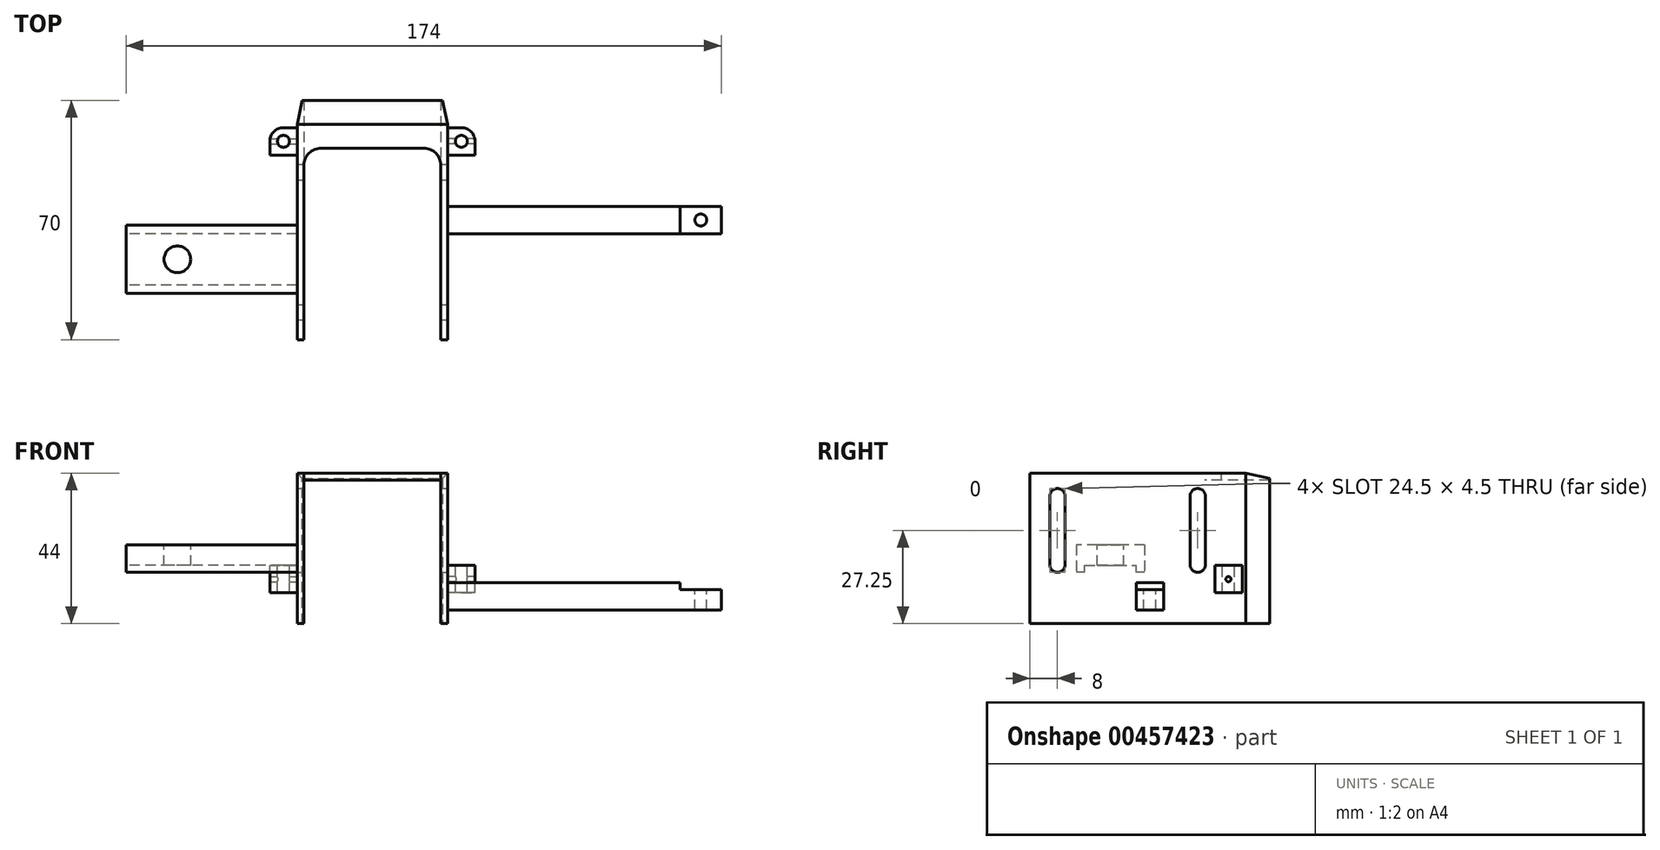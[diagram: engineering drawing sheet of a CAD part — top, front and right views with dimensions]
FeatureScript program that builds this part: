
annotation { "Feature Type Name" : "Feature", "Feature Type Description" : "" }
export const myFeature = defineFeature(function(context is Context, id is Id, definition is map)
    precondition{}
    {
        {
            var Q0;
            Q0=qCreatedBy(makeId("Front.planeOp"),FACE);
            var sketch = newSketch(context, id + "F0", { "sketchPlane" : qUnion([Q0])});
            skLineSegment(sketch, "E0.bottom", {"start": v(0, 0) * mm, "end": v(44, 0) * mm});
            skLineSegment(sketch, "E0.top", {"start": v(0, 44) * mm, "end": v(44, 44) * mm});
            skLineSegment(sketch, "E0.left", {"start": v(0, 0) * mm, "end": v(0, 44) * mm});
            skLineSegment(sketch, "E0.right", {"start": v(44, 0) * mm, "end": v(44, 44) * mm});
            skSolve(sketch);
        }
        {
            var Q0;
            Q0 = qSketchRegion(id + "F0", true);
            extrude(context, id + "F1", {"entities" : qUnion([Q0]), "oppositeDirection" : true, "depth" : 70 * mm});
        }
        {
            var Q0;
            Q0=makeQuery(id+"F1.opExtrude","CAP_FACE",FACE,{"disambiguationData":[OSD([sQuery(id+"F0.wireOp",EDGE,"E0.bottom"),sQuery(id+"F0.wireOp",EDGE,"E0.top"),sQuery(id+"F0.wireOp",EDGE,"E0.left"),sQuery(id+"F0.wireOp",EDGE,"E0.right")])],"isStart":true});
            var sketch = newSketch(context, id + "F2", { "sketchPlane" : qUnion([Q0])});
            skLineSegment(sketch, "E1.bottom", {"start": v(2, 0) * mm, "end": v(42, 0) * mm});
            skLineSegment(sketch, "E1.top", {"start": v(2, 42) * mm, "end": v(42, 42) * mm});
            skLineSegment(sketch, "E1.left", {"start": v(2, 0) * mm, "end": v(2, 42) * mm});
            skLineSegment(sketch, "E1.right", {"start": v(42, 0) * mm, "end": v(42, 42) * mm});
            skSolve(sketch);
        }
        {
            var Q0;
            Q0 = qSketchRegion(id + "F2", true);
            extrude(context, id + "F3", {"entities" : qUnion([Q0]), "operationType" : NewBodyOperationType.REMOVE, "endBound" : BoundingType.UP_TO_NEXT, "oppositeDirection" : true, "depth" : 25 * mm});
        }
        {
            var Q0;
            Q0=makeQuery(id+"F1.opExtrude","SWEPT_FACE",FACE,{"disambiguationData":[OSD([sQuery(id+"F0.wireOp",EDGE,"E0.right")])]});
            var sketch = newSketch(context, id + "F4", { "sketchPlane" : qUnion([Q0])});
            skLineSegment(sketch, "E2", {"start": v(46.75, 37.25) * mm, "end": v(46.75, 17.25) * mm});
            skLineSegment(sketch, "E3", {"start": v(51.25, 37.25) * mm, "end": v(51.25, 17.25) * mm});
            skArc(sketch, "E4", {"start": v(51.25, 37.25) * mm, "mid": v(49, 39.5) * mm, "end": v(46.75, 37.25) * mm});
            skArc(sketch, "E5", {"start": v(46.75, 17.25) * mm, "mid": v(49, 15) * mm, "end": v(51.25, 17.25) * mm});
            skSolve(sketch);
        }
        {
            var Q0;
            Q0 = qSketchRegion(id + "F4", true);
            extrude(context, id + "F5", {"entities" : qUnion([Q0]), "operationType" : NewBodyOperationType.REMOVE, "oppositeDirection" : true, "depth" : 44 * mm});
        }
        {
            var Q0;
            Q0=makeQuery(id+"F1.opExtrude","SWEPT_FACE",FACE,{"disambiguationData":[OSD([sQuery(id+"F0.wireOp",EDGE,"E0.top")])]});
            var sketch = newSketch(context, id + "F6", { "sketchPlane" : qUnion([Q0])});
            skLineSegment(sketch, "E6.bottom", {"start": v(2, 0) * mm, "end": v(42, 0) * mm});
            skLineSegment(sketch, "E6.top", {"start": v(7, 56) * mm, "end": v(37, 56) * mm});
            skLineSegment(sketch, "E6.left", {"start": v(2, 0) * mm, "end": v(2, 51) * mm});
            skLineSegment(sketch, "E6.right", {"start": v(42, 0) * mm, "end": v(42, 51) * mm});
            skPoint(sketch, "E7.visualSharp", {"position": v(2, 56) * mm});
            skArc(sketch, "E7.filletArc", {"start": v(7, 56) * mm, "mid": v(3.46, 54.54) * mm, "end": v(2, 51) * mm});
            skPoint(sketch, "E8.visualSharp", {"position": v(42, 56) * mm});
            skArc(sketch, "E8.filletArc", {"start": v(42, 51) * mm, "mid": v(40.54, 54.54) * mm, "end": v(37, 56) * mm});
            skSolve(sketch);
        }
        {
            var Q0;
            Q0=makeQuery(id+"F6.imprint","IMPRINT",FACE,{"disambiguationData":[TD([[makeQuery(id+"F6.imprint","IMPRINT",EDGE,{"derivedFrom":sQuery(id+"F6.wireOp",EDGE,"E6.bottom")}),1.0]])]});
            var Q1;
            Q1=sQuery(id+"F6.wireOp",EDGE,"E6.bottom");
            var Q2;
            Q2=sQuery(id+"F6.wireOp",EDGE,"E6.right");
            var Q3;
            Q3=sQuery(id+"F6.wireOp",EDGE,"E6.top");
            var Q4;
            Q4=sQuery(id+"F6.wireOp",EDGE,"E6.left");
            var Q5;
            Q5=sQuery(id+"F6.wireOp",EDGE,"E7.filletArc");
            var Q6;
            Q6=sQuery(id+"F6.wireOp",EDGE,"E8.filletArc");
            extrude(context, id + "F7", {"entities" : qUnion([Q0]), "operationType" : NewBodyOperationType.REMOVE, "surfaceEntities" : qUnion([Q1, Q2, Q3, Q4, Q5, Q6]), "endBound" : BoundingType.UP_TO_NEXT, "oppositeDirection" : true, "depth" : 25 * mm});
        }
        {
            var Q0;
            Q0=makeQuery(id+"F1.opExtrude","SWEPT_FACE",FACE,{"disambiguationData":[OSD([sQuery(id+"F0.wireOp",EDGE,"E0.right")])]});
            var sketch = newSketch(context, id + "F8", { "sketchPlane" : qUnion([Q0])});
            skLineSegment(sketch, "E9", {"start": v(5.75, 37.25) * mm, "end": v(5.75, 17.25) * mm});
            skLineSegment(sketch, "E10", {"start": v(10.25, 37.25) * mm, "end": v(10.25, 17.25) * mm});
            skArc(sketch, "E11", {"start": v(10.25, 37.25) * mm, "mid": v(8, 39.5) * mm, "end": v(5.75, 37.25) * mm});
            skArc(sketch, "E12", {"start": v(5.75, 17.25) * mm, "mid": v(8, 15) * mm, "end": v(10.25, 17.25) * mm});
            skSolve(sketch);
        }
        {
            var Q0;
            Q0=makeQuery(id+"F1.opExtrude","SWEPT_FACE",FACE,{"disambiguationData":[OSD([sQuery(id+"F0.wireOp",EDGE,"E0.right")])]});
            var sketch = newSketch(context, id + "F9", { "sketchPlane" : qUnion([Q0])});
            skLineSegment(sketch, "E13.bottom", {"start": v(39, 4) * mm, "end": v(31, 4) * mm});
            skLineSegment(sketch, "E13.top", {"start": v(39, 12) * mm, "end": v(31, 12) * mm});
            skLineSegment(sketch, "E13.left", {"start": v(39, 4) * mm, "end": v(39, 12) * mm});
            skLineSegment(sketch, "E13.right", {"start": v(31, 4) * mm, "end": v(31, 12) * mm});
            skPoint(sketch, "E13.middle", {"position": v(35, 8) * mm});
            skSolve(sketch);
        }
        {
            var Q0;
            Q0 = qSketchRegion(id + "F9", true);
            extrude(context, id + "F10", {"entities" : qUnion([Q0]), "operationType" : NewBodyOperationType.ADD, "depth" : 80 * mm});
        }
        {
            var Q0;
            Q0=makeQuery(id+"F10.opExtrude","CAP_FACE",FACE,{"disambiguationData":[OSD([sQuery(id+"F9.wireOp",EDGE,"E13.bottom"),sQuery(id+"F9.wireOp",EDGE,"E13.top"),sQuery(id+"F9.wireOp",EDGE,"E13.left"),sQuery(id+"F9.wireOp",EDGE,"E13.right")])],"isStart":false});
            var sketch = newSketch(context, id + "F11", { "sketchPlane" : qUnion([Q0])});
            skLineSegment(sketch, "E14.bottom", {"start": v(39, 12) * mm, "end": v(31, 12) * mm});
            skLineSegment(sketch, "E14.top", {"start": v(39, 10) * mm, "end": v(31, 10) * mm});
            skLineSegment(sketch, "E14.left", {"start": v(39, 12) * mm, "end": v(39, 10) * mm});
            skLineSegment(sketch, "E14.right", {"start": v(31, 12) * mm, "end": v(31, 10) * mm});
            skSolve(sketch);
        }
        {
            var Q0;
            Q0 = qSketchRegion(id + "F11", true);
            extrude(context, id + "F12", {"entities" : qUnion([Q0]), "operationType" : NewBodyOperationType.REMOVE, "oppositeDirection" : true, "depth" : 12 * mm});
        }
        {
            var Q0;
            Q0=makeQuery(id+"F1.opExtrude","SWEPT_FACE",FACE,{"disambiguationData":[OSD([sQuery(id+"F0.wireOp",EDGE,"E0.left")])]});
            var sketch = newSketch(context, id + "F13", { "sketchPlane" : qUnion([Q0])});
            skLineSegment(sketch, "E15.bottom", {"start": v(-33.5, 23) * mm, "end": v(-13.5, 23) * mm});
            skLineSegment(sketch, "E15.top", {"start": v(-33.5, 15) * mm, "end": v(-13.5, 15) * mm});
            skLineSegment(sketch, "E15.left", {"start": v(-33.5, 23) * mm, "end": v(-33.5, 15) * mm});
            skLineSegment(sketch, "E15.right", {"start": v(-13.5, 23) * mm, "end": v(-13.5, 15) * mm});
            skSolve(sketch);
        }
        {
            var Q0;
            Q0 = qSketchRegion(id + "F13", true);
            extrude(context, id + "F14", {"entities" : qUnion([Q0]), "operationType" : NewBodyOperationType.ADD, "depth" : 50 * mm});
        }
        {
            var Q0;
            Q0=makeQuery(id+"F14.opExtrude","CAP_FACE",FACE,{"disambiguationData":[OSD([sQuery(id+"F13.wireOp",EDGE,"E15.bottom"),sQuery(id+"F13.wireOp",EDGE,"E15.top"),sQuery(id+"F13.wireOp",EDGE,"E15.left"),sQuery(id+"F13.wireOp",EDGE,"E15.right")])],"isStart":false});
            var sketch = newSketch(context, id + "F15", { "sketchPlane" : qUnion([Q0])});
            skLineSegment(sketch, "E16.bottom", {"start": v(-16, 15) * mm, "end": v(-31, 15) * mm});
            skLineSegment(sketch, "E16.top", {"start": v(-16, 17) * mm, "end": v(-31, 17) * mm});
            skLineSegment(sketch, "E16.left", {"start": v(-16, 15) * mm, "end": v(-16, 17) * mm});
            skLineSegment(sketch, "E16.right", {"start": v(-31, 15) * mm, "end": v(-31, 17) * mm});
            skSolve(sketch);
        }
        {
            var Q0;
            Q0 = qSketchRegion(id + "F15", true);
            var Q1;
            Q1=makeQuery(id+"F1.opExtrude","SWEPT_FACE",FACE,{"disambiguationData":[OSD([sQuery(id+"F0.wireOp",EDGE,"E0.left")])]});
            extrude(context, id + "F16", {"entities" : qUnion([Q0]), "operationType" : NewBodyOperationType.REMOVE, "endBound" : BoundingType.UP_TO_SURFACE, "oppositeDirection" : true, "endBoundEntityFace" : qUnion([Q1]), "depth" : 46 * mm});
        }
        {
            var Q0;
            Q0=makeQuery(id+"F14.opExtrude","SWEPT_FACE",FACE,{"disambiguationData":[OSD([sQuery(id+"F13.wireOp",EDGE,"E15.bottom")])]});
            var sketch = newSketch(context, id + "F17", { "sketchPlane" : qUnion([Q0])});
            skCircle(sketch, "E17", {"center": v(-35, 23.5) * mm, "radius": 3.9 * mm});
            skPoint(sketch, "E17.centerSnap0", {"position": v(-50, 23.5) * mm});
            skSolve(sketch);
        }
        {
            var Q0;
            Q0 = qSketchRegion(id + "F17", true);
            extrude(context, id + "F18", {"entities" : qUnion([Q0]), "operationType" : NewBodyOperationType.REMOVE, "oppositeDirection" : true, "depth" : 20 * mm});
        }
        {
            var Q0;
            Q0=makeQuery(id+"F1.opExtrude","CAP_EDGE",EDGE,{"disambiguationData":[OSD([sQuery(id+"F0.wireOp",EDGE,"E0.right")])],"isStart":false});
            chamfer(context, id + "F19", {"entities" : qUnion([Q0]), "chamferType" : ChamferType.TWO_OFFSETS, "width1" : 7 * mm, "oppositeDirection" : false, "width2" : 1.5 * mm});
        }
        {
            var Q0;
            Q0=makeQuery(id+"F1.opExtrude","CAP_EDGE",EDGE,{"disambiguationData":[OSD([sQuery(id+"F0.wireOp",EDGE,"E0.top")])],"isStart":false});
            chamfer(context, id + "F20", {"entities" : qUnion([Q0]), "chamferType" : ChamferType.TWO_OFFSETS, "width1" : 1.5 * mm, "oppositeDirection" : false, "width2" : 7 * mm, "tangentPropagation" : true});
        }
        {
            var Q0;
            Q0=makeQuery(id+"F1.opExtrude","CAP_EDGE",EDGE,{"disambiguationData":[OSD([sQuery(id+"F0.wireOp",EDGE,"E0.left")])],"isStart":false});
            chamfer(context, id + "F21", {"entities" : qUnion([Q0]), "chamferType" : ChamferType.TWO_OFFSETS, "width1" : 1.5 * mm, "oppositeDirection" : false, "width2" : 7 * mm, "tangentPropagation" : true});
        }
        {
            var Q0;
            Q0=makeQuery(id+"F12.boolean.opBoolean","COPY",FACE,{"derivedFrom":makeQuery(id+"F12.opExtrude","SWEPT_FACE",FACE,{"disambiguationData":[OSD([sQuery(id+"F11.wireOp",EDGE,"E14.top")])]})});
            var sketch = newSketch(context, id + "F22", { "sketchPlane" : qUnion([Q0])});
            skCircle(sketch, "E18", {"center": v(118, 35) * mm, "radius": 1.75 * mm});
            skPoint(sketch, "E18.centerSnap0", {"position": v(124, 35) * mm});
            skSolve(sketch);
        }
        {
            var Q0;
            Q0 = qSketchRegion(id + "F22", true);
            extrude(context, id + "F23", {"entities" : qUnion([Q0]), "operationType" : NewBodyOperationType.REMOVE, "oppositeDirection" : true, "depth" : 8 * mm});
        }
        {
            var Q0;
            Q0 = qSketchRegion(id + "F8", true);
            extrude(context, id + "F24", {"entities" : qUnion([Q0]), "operationType" : NewBodyOperationType.REMOVE, "oppositeDirection" : true, "depth" : 44 * mm});
        }
        {
            var Q0;
            Q0=makeQuery(id+"F1.opExtrude","SWEPT_FACE",FACE,{"disambiguationData":[OSD([sQuery(id+"F0.wireOp",EDGE,"E0.right")])]});
            var sketch = newSketch(context, id + "F25", { "sketchPlane" : qUnion([Q0])});
            skLineSegment(sketch, "E19.bottom", {"start": v(62, 9) * mm, "end": v(54, 9) * mm});
            skLineSegment(sketch, "E19.top", {"start": v(62, 17) * mm, "end": v(54, 17) * mm});
            skLineSegment(sketch, "E19.left", {"start": v(62, 9) * mm, "end": v(62, 17) * mm});
            skLineSegment(sketch, "E19.right", {"start": v(54, 9) * mm, "end": v(54, 17) * mm});
            skPoint(sketch, "E19.middle", {"position": v(58, 13) * mm});
            skCircle(sketch, "E20", {"center": v(58, 13) * mm, "radius": 0.75 * mm});
            skSolve(sketch);
        }
        {
            var Q0;
            Q0=makeQuery(id+"F25.imprint","IMPRINT",FACE,{"disambiguationData":[TD([[makeQuery(id+"F25.imprint","IMPRINT",EDGE,{"derivedFrom":sQuery(id+"F25.wireOp",EDGE,"E19.bottom")}),-1.0]])]});
            extrude(context, id + "F26", {"entities" : qUnion([Q0]), "operationType" : NewBodyOperationType.ADD, "depth" : 8 * mm});
        }
        {
            var Q0;
            Q0=makeQuery(id+"F26.opExtrude","SWEPT_FACE",FACE,{"disambiguationData":[OSD([sQuery(id+"F25.wireOp",EDGE,"E19.top")])]});
            var sketch = newSketch(context, id + "F27", { "sketchPlane" : qUnion([Q0])});
            skCircle(sketch, "E21", {"center": v(48, 58) * mm, "radius": 1.75 * mm});
            skPoint(sketch, "E21.centerSnap0", {"position": v(48, 62) * mm});
            skSolve(sketch);
        }
        {
            var Q0;
            Q0 = qSketchRegion(id + "F27", true);
            extrude(context, id + "F28", {"entities" : qUnion([Q0]), "operationType" : NewBodyOperationType.REMOVE, "oppositeDirection" : true, "depth" : 8 * mm});
        }
        {
            var Q0;
            Q0=makeQuery(id+"F26.opExtrude","CAP_EDGE",EDGE,{"disambiguationData":[OSD([sQuery(id+"F25.wireOp",EDGE,"E19.left")])],"isStart":false});
            fillet(context, id + "F29", {"entities" : qUnion([Q0]), "radius" : 4 * mm, "tangentPropagation" : true, "allowEdgeOverflow" : false});
        }
        {
            var Q0;
            Q0=makeQuery(id+"F16.boolean.opBoolean","MERGE",FACE,{"derivedFrom":[makeQuery(id+"F1.opExtrude","SWEPT_FACE",FACE,{"disambiguationData":[OSD([sQuery(id+"F0.wireOp",EDGE,"E0.left")])]}),makeQuery(id+"F16.opExtrude","CAP_FACE",FACE,{"disambiguationData":[OSD([sQuery(id+"F15.wireOp",EDGE,"E16.bottom"),sQuery(id+"F15.wireOp",EDGE,"E16.top"),sQuery(id+"F15.wireOp",EDGE,"E16.left"),sQuery(id+"F15.wireOp",EDGE,"E16.right")])],"isStart":false})]});
            var sketch = newSketch(context, id + "F30", { "sketchPlane" : qUnion([Q0])});
            skLineSegment(sketch, "E22.bottom", {"start": v(-54, 9) * mm, "end": v(-62, 9) * mm});
            skLineSegment(sketch, "E22.top", {"start": v(-54, 17) * mm, "end": v(-62, 17) * mm});
            skLineSegment(sketch, "E22.left", {"start": v(-54, 9) * mm, "end": v(-54, 17) * mm});
            skLineSegment(sketch, "E22.right", {"start": v(-62, 9) * mm, "end": v(-62, 17) * mm});
            skPoint(sketch, "E22.middle", {"position": v(-58, 13) * mm});
            skCircle(sketch, "E23", {"center": v(-58, 13) * mm, "radius": 0.75 * mm});
            skSolve(sketch);
        }
        {
            var Q0;
            Q0 = qSketchRegion(id + "F30", true);
            extrude(context, id + "F31", {"entities" : qUnion([Q0]), "operationType" : NewBodyOperationType.ADD, "depth" : 8 * mm});
        }
        {
            var Q0;
            Q0=makeQuery(id+"F31.opExtrude","SWEPT_FACE",FACE,{"disambiguationData":[OSD([sQuery(id+"F30.wireOp",EDGE,"E22.top")])]});
            var sketch = newSketch(context, id + "F32", { "sketchPlane" : qUnion([Q0])});
            skCircle(sketch, "E24", {"center": v(-4, 58) * mm, "radius": 1.75 * mm});
            skPoint(sketch, "E24.centerSnap0", {"position": v(-4, 62) * mm});
            skSolve(sketch);
        }
        {
            var Q0;
            Q0 = qSketchRegion(id + "F32", true);
            extrude(context, id + "F33", {"entities" : qUnion([Q0]), "operationType" : NewBodyOperationType.REMOVE, "oppositeDirection" : true, "depth" : 8 * mm});
        }
        {
            var Q0;
            Q0=makeQuery(id+"F31.opExtrude","CAP_EDGE",EDGE,{"disambiguationData":[OSD([sQuery(id+"F30.wireOp",EDGE,"E22.right")])],"isStart":false});
            fillet(context, id + "F34", {"entities" : qUnion([Q0]), "radius" : 4 * mm, "tangentPropagation" : true, "allowEdgeOverflow" : false});
        }
    });
